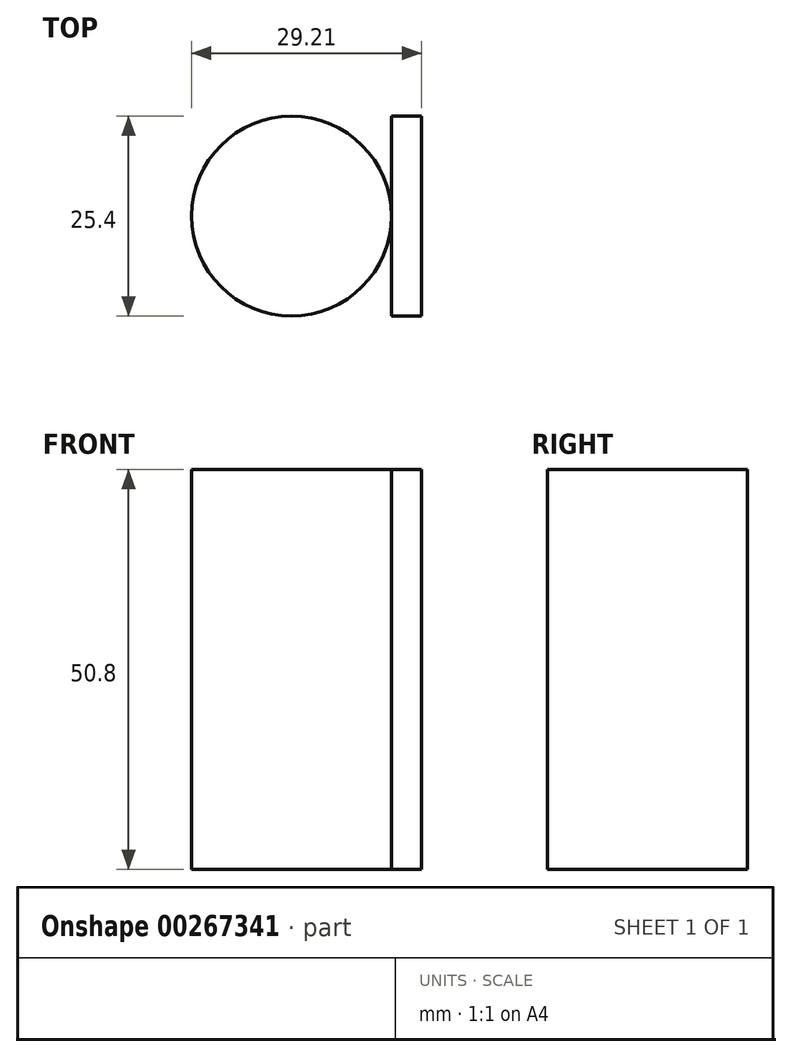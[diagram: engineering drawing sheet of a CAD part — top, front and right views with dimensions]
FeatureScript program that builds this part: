
annotation { "Feature Type Name" : "Feature", "Feature Type Description" : "" }
export const myFeature = defineFeature(function(context is Context, id is Id, definition is map)
    precondition{}
    {
        {
            var Q0;
            Q0=qCreatedBy(makeId("Top.planeOp"),FACE);
            var sketch = newSketch(context, id + "F0", { "sketchPlane" : qUnion([Q0])});
            skCircle(sketch, "E0", {"center": v(0, 0) * mm, "radius": 12.7 * mm});
            skSolve(sketch);
        }
        {
            var Q0;
            Q0=makeQuery(id+"F0.imprint","IMPRINT",FACE,{"disambiguationData":[TD([[makeQuery(id+"F0.imprint","IMPRINT",EDGE,{"derivedFrom":sQuery(id+"F0.wireOp",EDGE,"E0")}),1.0]])]});
            extrude(context, id + "F1", {"entities" : qUnion([Q0]), "depth" : 50.8 * mm});
        }
        {
            var Q0;
            Q0=qCreatedBy(makeId("Right.planeOp"),FACE);
            cPlane(context, id + "F2", {"entities" : qUnion([Q0]), "cplaneType" : CPlaneType.OFFSET, "offset" : 12.7 * mm, "width" : 152.4 * mm, "height" : 152.4 * mm});
        }
        {
            var Q0;
            Q0=qCreatedBy(id+"F2.planeOp",FACE);
            var sketch = newSketch(context, id + "F3", { "sketchPlane" : qUnion([Q0])});
            skLineSegment(sketch, "E1.bottom", {"start": v(12.7, 0) * mm, "end": v(-12.7, 0) * mm});
            skLineSegment(sketch, "E1.top", {"start": v(12.7, 50.8) * mm, "end": v(-12.7, 50.8) * mm});
            skLineSegment(sketch, "E1.left", {"start": v(12.7, 0) * mm, "end": v(12.7, 50.8) * mm});
            skLineSegment(sketch, "E1.right", {"start": v(-12.7, 0) * mm, "end": v(-12.7, 50.8) * mm});
            skPoint(sketch, "E1.middle", {"position": v(0, 25.4) * mm});
            skSolve(sketch);
        }
        {
            var Q0;
            Q0=makeQuery(id+"F3.imprint","IMPRINT",FACE,{"disambiguationData":[TD([[makeQuery(id+"F3.imprint","IMPRINT",EDGE,{"derivedFrom":sQuery(id+"F3.wireOp",EDGE,"E1.bottom")}),-1.0]])]});
            extrude(context, id + "F4", {"entities" : qUnion([Q0]), "operationType" : NewBodyOperationType.ADD, "depth" : 3.8 * mm});
        }
    });
